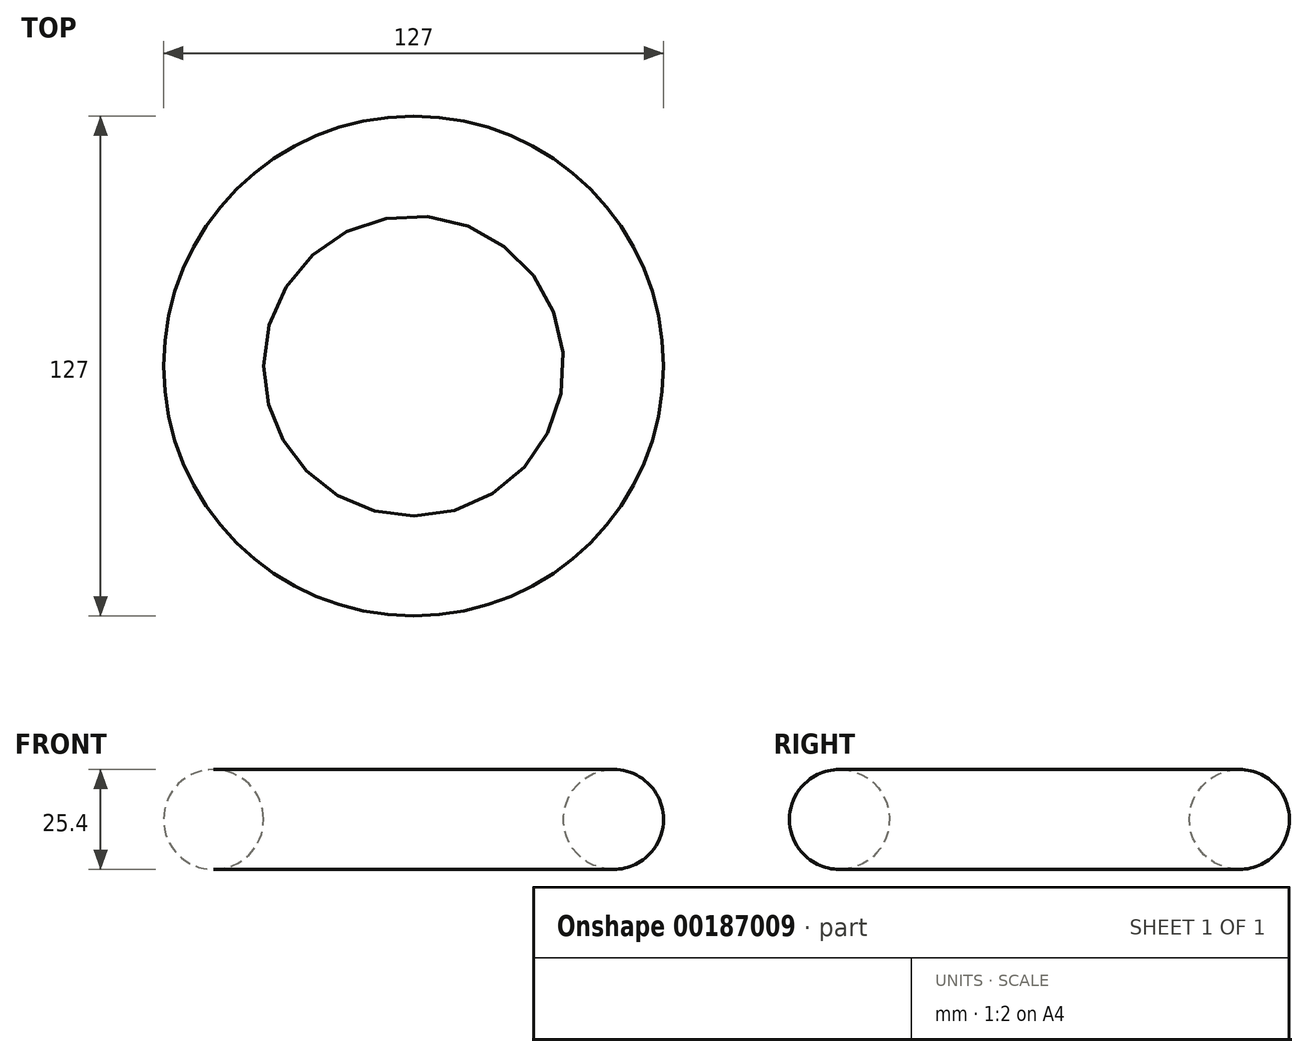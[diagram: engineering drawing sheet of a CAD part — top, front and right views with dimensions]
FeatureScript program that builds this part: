
annotation { "Feature Type Name" : "Feature", "Feature Type Description" : "" }
export const myFeature = defineFeature(function(context is Context, id is Id, definition is map)
    precondition{}
    {
        {
            var Q0;
            Q0=qCreatedBy(makeId("Front.planeOp"),FACE);
            var sketch = newSketch(context, id + "F0", { "sketchPlane" : qUnion([Q0])});
            skCircle(sketch, "E0", {"center": v(50.8, 0) * mm, "radius": 12.7 * mm});
            skLineSegment(sketch, "E1", {"start": v(0, 0) * mm, "end": v(0, 28.94) * mm});
            skSolve(sketch);
        }
        {
            var Q0;
            Q0=makeQuery(id+"F0.imprint","IMPRINT",FACE,{"disambiguationData":[TD([[makeQuery(id+"F0.imprint","IMPRINT",EDGE,{"derivedFrom":sQuery(id+"F0.wireOp",EDGE,"E0")}),1.0]])]});
            var Q1;
            Q1=sQuery(id+"F0.wireOp",EDGE,"E1");
            revolve(context, id + "F1", {"entities" : qUnion([Q0]), "axis" : qUnion([Q1]), "revolveType" : RevolveType.FULL});
        }
    });
